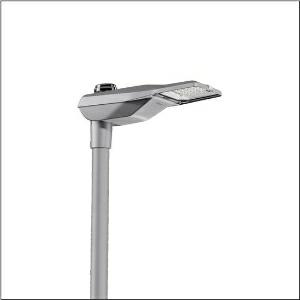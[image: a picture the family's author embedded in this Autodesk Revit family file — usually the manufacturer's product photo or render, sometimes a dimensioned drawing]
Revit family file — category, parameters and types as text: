
# Revit family: streetlight_sl_21_micro___p0_8a_5xe5u27n08cb_fa48
name_source: partatom
category: Lighting Fixtures
units: mm (PartAtom-declared; Revit-internal decimal feet)

## family parameters
Cut with Voids When Loaded = No
Host = Face
Light Source = No
Part Type = Normal
Room Calculation Point = No
Round Connector Dimension = Use Diameter
Shared = No

## types (1)
- --- (1 x LED, 1870 lm, 15.8 W, 2200K)
    Apparent Load = 16 VA
    CIE Flux Codes = 33 69 96 100 100
    Color Rendering = 70
    Color Temperature = 2200K
    Default Elevation = 1800 mm
    Description = Streetlight SL 21 micro, mast luminaire, primary light control with lens, of PMMA, primary optical cover: cover, of toughened safety glass, transparent, light distribution: P0.8a, light emission: direct distribution, primary light characteristic: asymmetric, installation type: post-top, LED, 3G 1.5mm², High Power LED, rated luminous flux: 1.870lm, luminous efficacy: 118lm/W, light colour: 722, colour temperature: 2200K, control gear: NEMA (7pin), control: flexible luminous flux parameterisation, time-dependent luminous flux control, constant luminous flux control, pre-setting: linear dimming characteristic, overheat protection, mains connection: 230..240V, AC, 50/60Hz, connection cable pre-assembled, cable length: 6,5m, wiring characteristics: H07RN-F, start of lifetime: 16W, end of service life: 16W, reduction: 8W, luminaire housing, of diecast aluminium (EN AC-44300), powder-coated, Siteco® metallic grey (DB 702S), corrosivity category C5 mid according to DIN EN ISO 12944, multi-level sealing system, sealing non-destructively replaceable, inclination adjustable: 0°, 5°, 10°, 15°, length: 528mm, width: 235mm, height: 110mm, spigot size: 76/60mm (post-top), mounting height: 4..8m, protection rating (complete): IP66, insulation class (complete): insulation class I (protective earthing), certification: CE, ENEC, ENEC+, VDE, impact resistance: IK10, permissible operating ambient temperature for outdoor applications: -40..+50°C, standard-compliant lighting for roads and squares, packaging unit: 1 piece

Light Distribution: P0.8a
    Height = 110 mm
    Lamp = 1 x LED
    Lamp Light Flux = 1870 lm
    Lamp Power = 15.8 W
    Lamp count = 1
    Length = 528 mm
    Luminous efficacy = 118 lm/W
    Manufacturer = Siteco
    ModVariant = No
    Model = 5XE5U27N08CB
    Number of Poles = 1
    OnlyDefault = Yes
    Power Factor = 1
    Product Name = Streetlight SL 21 micro | P0.8a
    Product group = mast luminaire | pylon top
    ProductGroupID = 6100
    Protection Class = Protection class I
    Protection Degree = IP 66
    RLX_Detail_Level = 1
    RLX_Emergency_Light_Flux = 0 lm
    RLX_Emergency_Type = 0
    RLX_Emergency_Type_DB = No
    RlxData = <blob elided: 99129 chars, md5=d55faabd>
    Socket = socket
    Standby Power = 0 W
    System Light Flux = 1870 lm
    System Power = 16 W
    Type Comments = factory setting: luminous flux: 100 % | dim-lin: 254 | 300 mA
    Type Image = l_1294375.jpg
    URL = http://relux.com
    VarID = @adj_095399
    Voltage = 0 V
    Weight = 0.00 kg
    Width = 235 mm

## geometry (parser evidence)
native form markers: Blend x4, Sweep x9
no freeform markers — native parametric forms only
